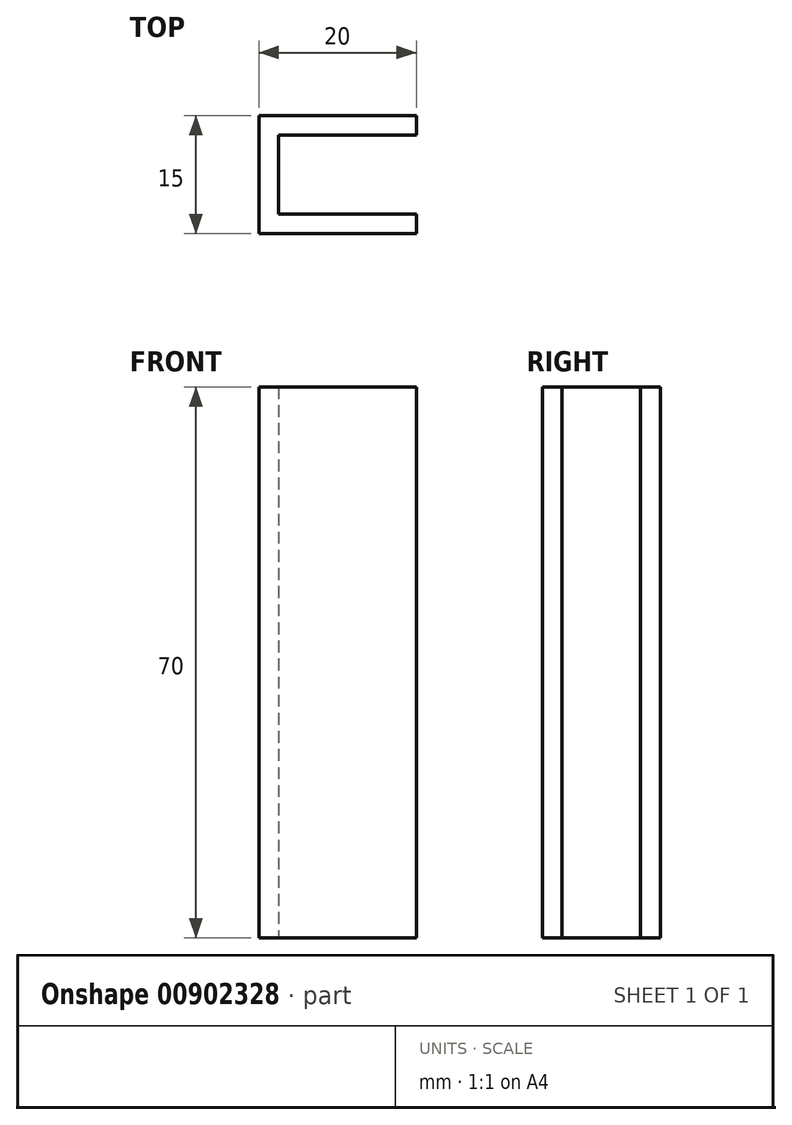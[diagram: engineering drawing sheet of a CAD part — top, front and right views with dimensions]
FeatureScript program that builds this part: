
annotation { "Feature Type Name" : "Feature", "Feature Type Description" : "" }
export const myFeature = defineFeature(function(context is Context, id is Id, definition is map)
    precondition{}
    {
        {
            var Q0;
            Q0=qCreatedBy(makeId("Front.planeOp"),FACE);
            var sketch = newSketch(context, id + "F0", { "sketchPlane" : qUnion([Q0])});
            skLineSegment(sketch, "E0.bottom", {"start": v(-10, 35) * mm, "end": v(10, 35) * mm});
            skLineSegment(sketch, "E0.top", {"start": v(-10, -35) * mm, "end": v(10, -35) * mm});
            skLineSegment(sketch, "E0.left", {"start": v(-10, 35) * mm, "end": v(-10, -35) * mm});
            skLineSegment(sketch, "E0.right", {"start": v(10, 35) * mm, "end": v(10, -35) * mm});
            skPoint(sketch, "E0.middle", {"position": v(0, 0) * mm});
            skSolve(sketch);
        }
        {
            var Q0;
            Q0=makeQuery(id+"F0.imprint","IMPRINT",FACE,{"disambiguationData":[TD([[makeQuery(id+"F0.imprint","IMPRINT",EDGE,{"derivedFrom":sQuery(id+"F0.wireOp",EDGE,"E0.bottom")}),-1.0]])]});
            extrude(context, id + "F1", {"entities" : qUnion([Q0]), "depth" : 15 * mm, "offsetDistance" : 25 * mm});
        }
        {
            var Q0;
            Q0=makeQuery(id+"F1.opExtrude","SWEPT_FACE",FACE,{"disambiguationData":[OSD([sQuery(id+"F0.wireOp",EDGE,"E0.right")])]});
            var Q1;
            Q1=makeQuery(id+"F1.opExtrude","SWEPT_FACE",FACE,{"disambiguationData":[OSD([sQuery(id+"F0.wireOp",EDGE,"E0.top")])]});
            var Q2;
            Q2=makeQuery(id+"F1.opExtrude","SWEPT_FACE",FACE,{"disambiguationData":[OSD([sQuery(id+"F0.wireOp",EDGE,"E0.bottom")])]});
            shell(context, id + "F2", {"entities" : qUnion([Q0, Q1, Q2]), "thickness" : 2.5 * mm});
        }
    });
